# Revit family: AFX-Irvine_Led-Outdoor_Sconce
name_source: partatom
category: Lighting Fixtures
units: mm (PartAtom-declared; Revit-internal decimal feet)

## family parameters
Cut with Voids When Loaded = No
Host = Face
Light Source = Yes
Part Type = Normal
Room Calculation Point = No
Round Connector Dimension = Use Diameter
Shared = No

## types (2) — shared parameters
Apparent Load = 0 VA
Assembly Code = D5020200
Canopy Finish = AFX - Black Steel
Color Filter = 16777215
Colour Rendering Index = 80
Cover Finish = AFX - Black Steel
Default Elevation = 48"
Diffuser Finish = AFX - White Acrylic
Dimming Lamp Color Temperature Shift = <None>
Housing Finish = AFX - Black Steel
Keynote = 12500
Manufacturer = AFX Inc
Photometric Web File = IRVW0408LAJUDBK(3000K).IES
Power Factor = 1
Product Documentation Link = https://www.afxinc.com
Revit File Built By = https://servex-us.com
Sustainability = https://lamprecycle.org
Tilt Angle = 90.00°
Type Comments = Irvine
URL = https://www.afxinc.com
Voltage = 120 V

## per-type parameters (varying)
| type | 12" | 8" | Depth | Description | Height | Wattage Comments | Width |
| IRVW0408LAJUDBK | No | Yes | 5" | Led Outdoor Sconce - 4 3/4"W x 5"D x 8"H | 8" | 8 | 4 3/4" |
| IRVW0512LAJUDBK | Yes | No | 6 1/2" | Led Outdoor Sconce - 5 3/8"W x 6 1/2"D x 12"H | 12" | 15 | 5 3/8" |

note: column(s) folded — value = type name in every type: Model

## geometry (parser evidence)
native form markers: Sweep x5
no freeform markers — native parametric forms only
